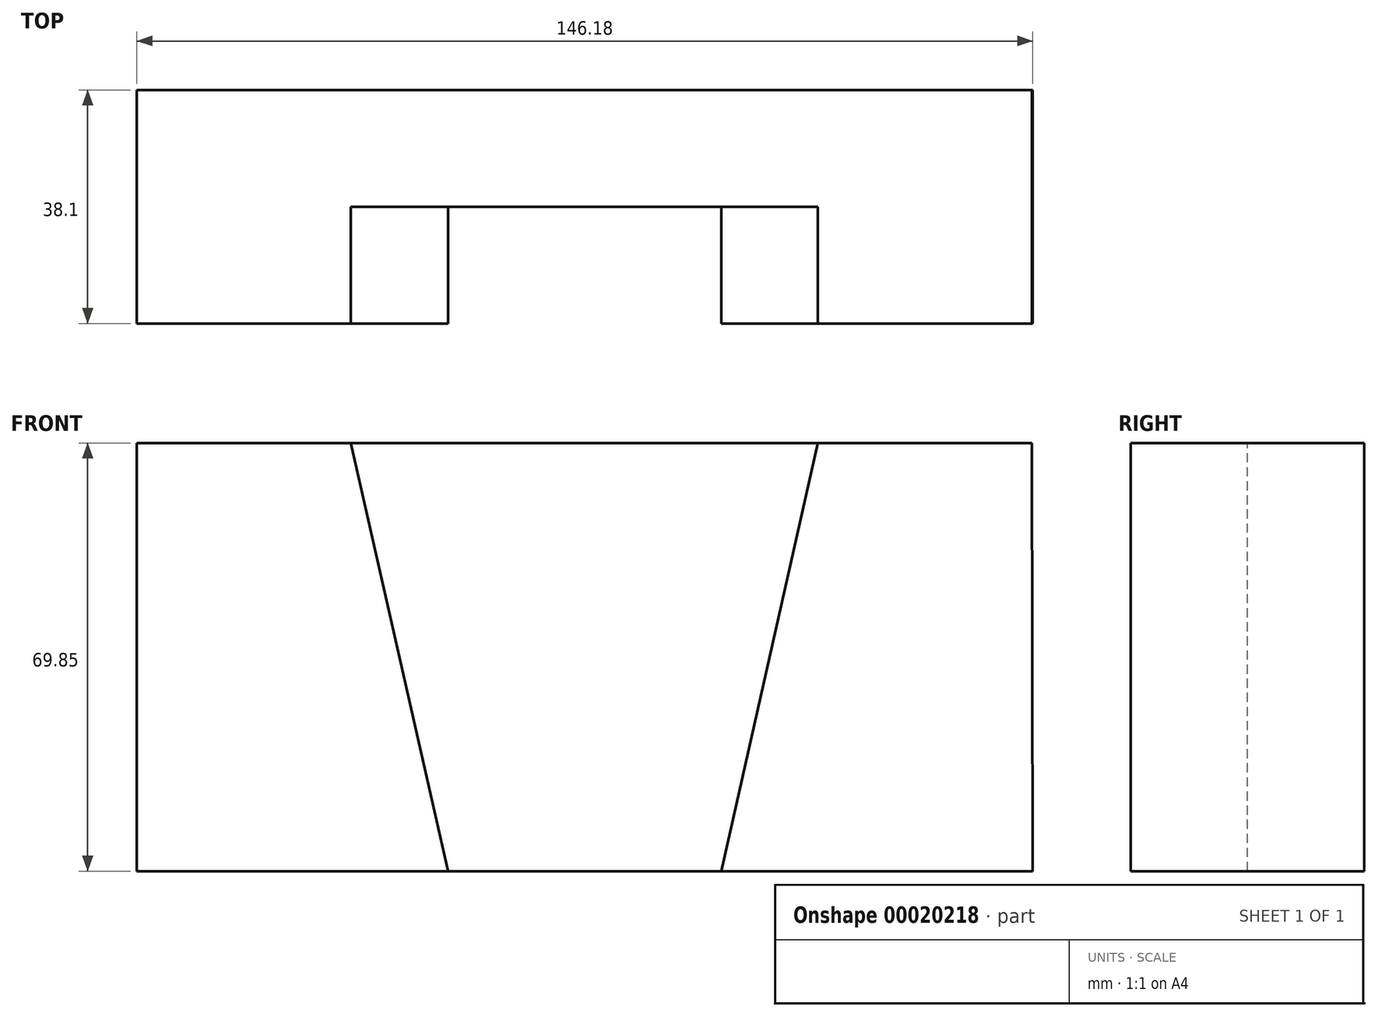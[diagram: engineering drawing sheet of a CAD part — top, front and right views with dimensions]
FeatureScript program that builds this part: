
annotation { "Feature Type Name" : "Feature", "Feature Type Description" : "" }
export const myFeature = defineFeature(function(context is Context, id is Id, definition is map)
    precondition{}
    {
        {
            var Q0;
            Q0=qCreatedBy(makeId("Front.planeOp"),FACE);
            var sketch = newSketch(context, id + "F0", { "sketchPlane" : qUnion([Q0])});
            skLineSegment(sketch, "E0", {"start": v(38.55, 49.14) * mm, "end": v(73.47, 49.14) * mm});
            skLineSegment(sketch, "E1", {"start": v(-72.58, 49.14) * mm, "end": v(-72.58, -20.71) * mm});
            skLineSegment(sketch, "E2", {"start": v(22.8, -20.71) * mm, "end": v(73.6, -20.71) * mm});
            skLineSegment(sketch, "E3", {"start": v(73.47, 49.14) * mm, "end": v(73.6, -20.71) * mm});
            skLineSegment(sketch, "E4", {"start": v(73.6, -20.71) * mm, "end": v(22.8, -20.71) * mm});
            skLineSegment(sketch, "E5", {"start": v(73.47, 49.14) * mm, "end": v(38.55, 49.14) * mm});
            skLineSegment(sketch, "E6", {"start": v(-72.58, -20.71) * mm, "end": v(-21.78, -20.71) * mm});
            skLineSegment(sketch, "E7", {"start": v(-72.58, 49.14) * mm, "end": v(-37.65, 49.14) * mm});
            skLineSegment(sketch, "E8", {"start": v(-37.65, 49.14) * mm, "end": v(38.55, 49.14) * mm});
            skLineSegment(sketch, "E9", {"start": v(38.55, 49.14) * mm, "end": v(22.8, -20.71) * mm});
            skLineSegment(sketch, "E10", {"start": v(-21.78, -20.71) * mm, "end": v(22.8, -20.71) * mm});
            skLineSegment(sketch, "E11", {"start": v(-21.78, -20.71) * mm, "end": v(-37.65, 49.14) * mm});
            skSolve(sketch);
        }
        {
            var Q0;
            Q0=makeQuery(id+"F0.imprint","IMPRINT",FACE,{"disambiguationData":[TD([[makeQuery(id+"F0.imprint","IMPRINT",EDGE,{"derivedFrom":sQuery(id+"F0.wireOp",EDGE,"E1")}),1.0]])]});
            extrude(context, id + "F1", {"entities" : qUnion([Q0]), "depth" : 38.1 * mm});
        }
        {
            var Q0;
            Q0=makeQuery(id+"F0.imprint","IMPRINT",FACE,{"disambiguationData":[TD([[makeQuery(id+"F0.imprint","IMPRINT",EDGE,{"derivedFrom":sQuery(id+"F0.wireOp",EDGE,"E8")}),-1.0]])]});
            extrude(context, id + "F2", {"entities" : qUnion([Q0]), "operationType" : NewBodyOperationType.ADD, "depth" : 19.05 * mm});
        }
        {
            var Q0;
            Q0=makeQuery(id+"F0.imprint","IMPRINT",FACE,{"disambiguationData":[TD([[makeQuery(id+"F0.imprint","IMPRINT",EDGE,{"derivedFrom":sQuery(id+"F0.wireOp",EDGE,"E3")}),-1.0]])]});
            extrude(context, id + "F3", {"entities" : qUnion([Q0]), "operationType" : NewBodyOperationType.ADD, "depth" : 38.1 * mm});
        }
    });
